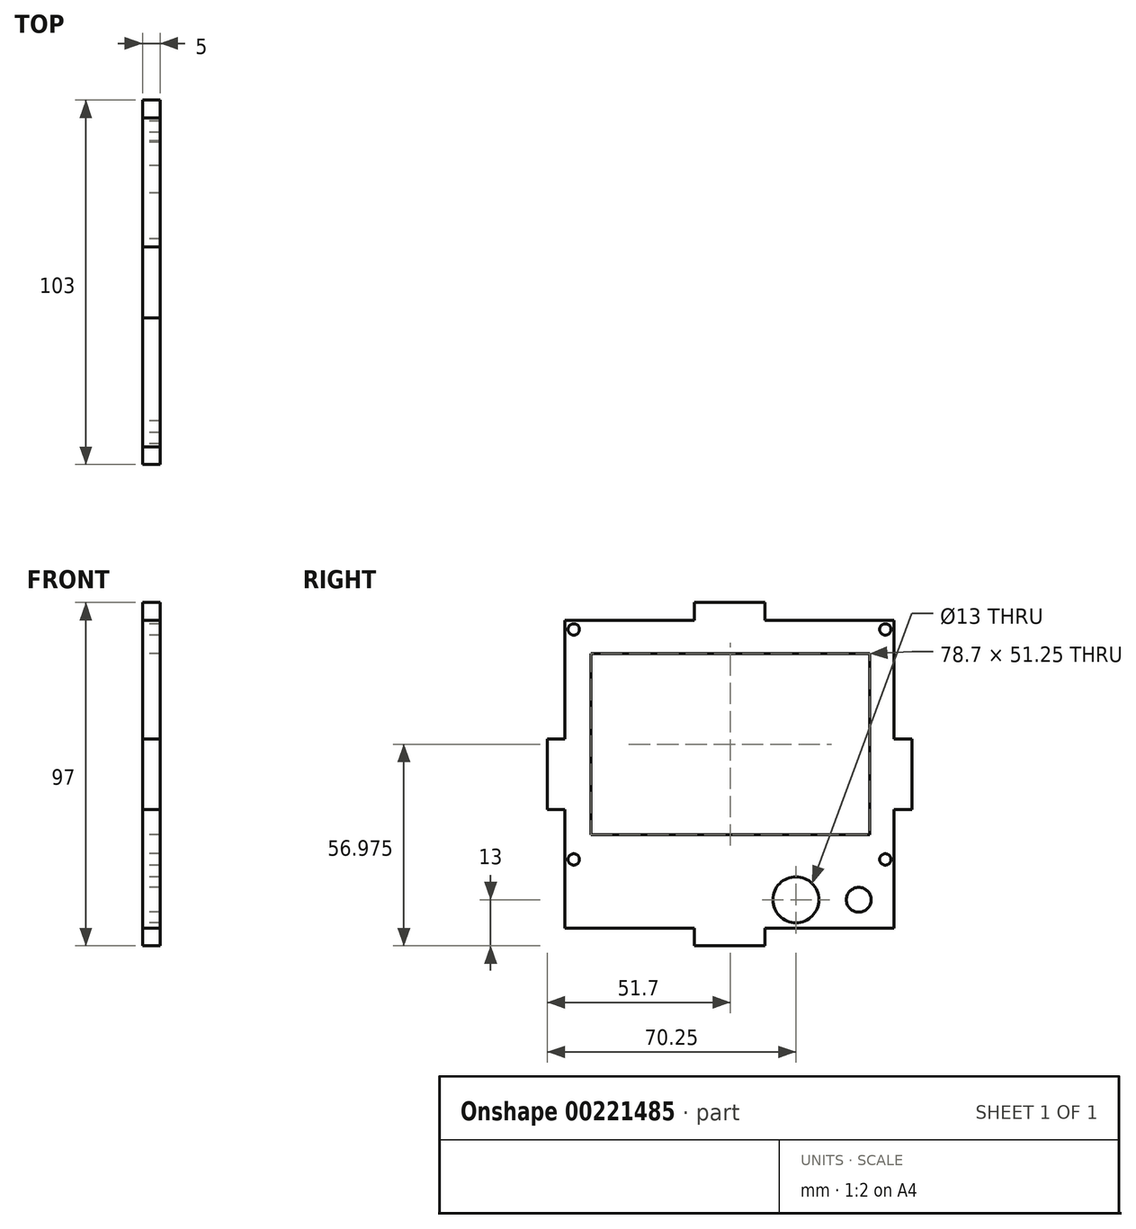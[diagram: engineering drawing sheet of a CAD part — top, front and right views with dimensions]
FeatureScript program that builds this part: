
annotation { "Feature Type Name" : "Feature", "Feature Type Description" : "" }
export const myFeature = defineFeature(function(context is Context, id is Id, definition is map)
    precondition{}
    {
        {
            assignVariable(context, id + "F0", {"name" : "thickness", "anyValue" : 5 * mm});
        }
        {
            var Q0;
            Q0=qCreatedBy(makeId("Right.planeOp"),FACE);
            var sketch = newSketch(context, id + "F1", { "sketchPlane" : qUnion([Q0])});
            skLineSegment(sketch, "E0.bottom", {"start": v(0, 87) * mm, "end": v(93, 87) * mm});
            skLineSegment(sketch, "E0.top", {"start": v(0, 0) * mm, "end": v(93, 0) * mm});
            skLineSegment(sketch, "E0.left", {"start": v(0, 87) * mm, "end": v(0, 0) * mm});
            skLineSegment(sketch, "E0.right", {"start": v(93, 87) * mm, "end": v(93, 0) * mm});
            skPoint(sketch, "E1.centerSnap0", {"position": v(0, 43.5) * mm});
            skLineSegment(sketch, "E2", {"start": v(-5, 53.5) * mm, "end": v(0, 53.5) * mm});
            skLineSegment(sketch, "E3", {"start": v(-5, 33.5) * mm, "end": v(0, 33.5) * mm});
            skLineSegment(sketch, "E4.trimOffspring", {"start": v(-5, 53.5) * mm, "end": v(-5, 33.5) * mm});
            skLineSegment(sketch, "E5", {"start": v(46.5, 92) * mm, "end": v(46.5, -5) * mm, "construction": true});
            skLineSegment(sketch, "E6", {"start": v(93, 43.5) * mm, "end": v(0, 43.5) * mm, "construction": true});
            skLineSegment(sketch, "E7.MirrorCS", {"start": v(98, 53.5) * mm, "end": v(93, 53.5) * mm});
            skLineSegment(sketch, "E8.MirrorCS", {"start": v(98, 53.5) * mm, "end": v(98, 33.5) * mm});
            skLineSegment(sketch, "E9.MirrorCS", {"start": v(98, 33.5) * mm, "end": v(93, 33.5) * mm});
            skPoint(sketch, "E10.MirrorP", {"position": v(93, 43.5) * mm});
            skLineSegment(sketch, "E11.bottom", {"start": v(7.35, 77.6) * mm, "end": v(86.05, 77.6) * mm});
            skLineSegment(sketch, "E11.top", {"start": v(7.35, 26.35) * mm, "end": v(86.05, 26.35) * mm});
            skLineSegment(sketch, "E11.left", {"start": v(7.35, 77.6) * mm, "end": v(7.35, 26.35) * mm});
            skLineSegment(sketch, "E11.right", {"start": v(86.05, 77.6) * mm, "end": v(86.05, 26.35) * mm});
            skCircle(sketch, "E12", {"center": v(83, 8) * mm, "radius": 3.5 * mm});
            skCircle(sketch, "E13", {"center": v(65.25, 8) * mm, "radius": 6.5 * mm});
            skLineSegment(sketch, "E14", {"start": v(36.5, 92) * mm, "end": v(36.5, 87) * mm});
            skLineSegment(sketch, "E15", {"start": v(56.5, 92) * mm, "end": v(56.5, 87) * mm});
            skLineSegment(sketch, "E16.trimOffspring", {"start": v(36.5, 92) * mm, "end": v(56.5, 92) * mm});
            skLineSegment(sketch, "E17.MirrorCS", {"start": v(56.5, -5) * mm, "end": v(56.5, 0) * mm});
            skLineSegment(sketch, "E18.MirrorCS", {"start": v(36.5, -5) * mm, "end": v(56.5, -5) * mm});
            skLineSegment(sketch, "E19.MirrorCS", {"start": v(36.5, -5) * mm, "end": v(36.5, 0) * mm});
            skCircle(sketch, "E20", {"center": v(2.5, 19.4) * mm, "radius": 1.6 * mm});
            skCircle(sketch, "E21", {"center": v(2.5, 84.4) * mm, "radius": 1.6 * mm});
            skCircle(sketch, "E22", {"center": v(90.5, 84.4) * mm, "radius": 1.6 * mm});
            skCircle(sketch, "E23", {"center": v(90.5, 19.4) * mm, "radius": 1.6 * mm});
            skLineSegment(sketch, "E24", {"start": v(2.5, 84.4) * mm, "end": v(90.5, 84.4) * mm, "construction": true});
            skPoint(sketch, "E25", {"position": v(46.5, 84.4) * mm});
            skSolve(sketch);
        }
        {
            var Q0;
            Q0 = qSketchRegion(id + "F1", true);
            extrude(context, id + "F2", {"entities" : qUnion([Q0]), "depth" : getVariable(context, 'thickness')});
        }
    });
